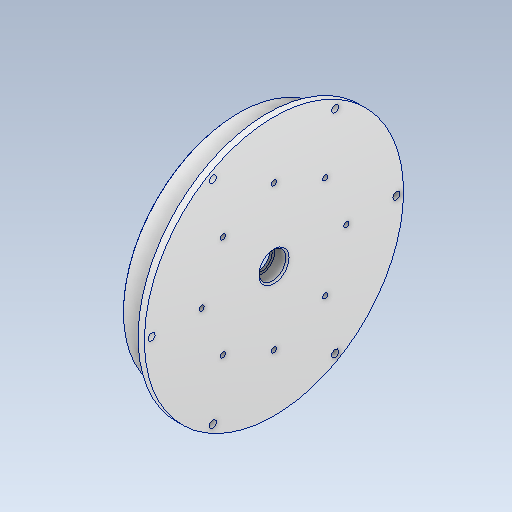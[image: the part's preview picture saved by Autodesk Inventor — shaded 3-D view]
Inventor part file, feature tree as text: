
AUTODESK INVENTOR PART (.ipt)
format: ipt  version: 2021 (Build 250183000, 183)  size: 208,384 bytes
history: native  units: mm
features: sketch x3, chamfer x2, hole x2, revolve x1, pattern_circular x1, projected_geometry x1
ambient origin geometry x8: Origin, YZ Plane, XZ Plane, XY Plane, X Axis, Y Axis, Z Axis, Center Point
bodies: Solid1 (feature_tree)
feature tree (10):
  revolve  "Revolution1"  Angle=90.0deg
  chamfer  "Chamfer1"  Distance=1.0mm Angle=45.0deg
  hole  "Hole1"  [1 undecoded]
  pattern_circular  "Circular Pattern1"  [2 undecoded]
  chamfer  "Chamfer2"  Distance=6.0mm
  hole  "Hole2"  [1 undecoded]
  sketch  "Sketch1"  dims[d7=8.5mm d11=90.0deg]
  sketch  "Sketch2"  dims[d15=1.5mm]
  projected_geometry  "Projected Loop1"
  sketch  "Sketch3"  dims[d18=1.625mm d19=1.0mm d20=2.0mm d21=45.0deg d23=13.1mm d25=64.0mm d26=6.0mm d27=50.0mm d28=4.92233mm d29=3.5mm d30=4.0mm d31=9.0mm d33=4.5mm d34=4.5mm d35=4.5mm d36=8.0mm d37=9.4mm d38=2.0mm d39=90.0deg d40=8.0mm d41=20.594885mm d42=60.0mm d43=360.0deg d45=0.4mm d46=2.0mm d47=45.0deg d48=91.0mm d49=80.0mm d51=360.0deg d53=3.242mm d54=8.0mm d55=4.0mm d56=2.0mm d57=90.0deg d58=11.8mm d59=20.594885mm]
note: 4 required parameter values undecoded (feature->parameter linkage not recoverable at this tier; creation-order binding heuristic only, values carry confidence <= 0.55)
